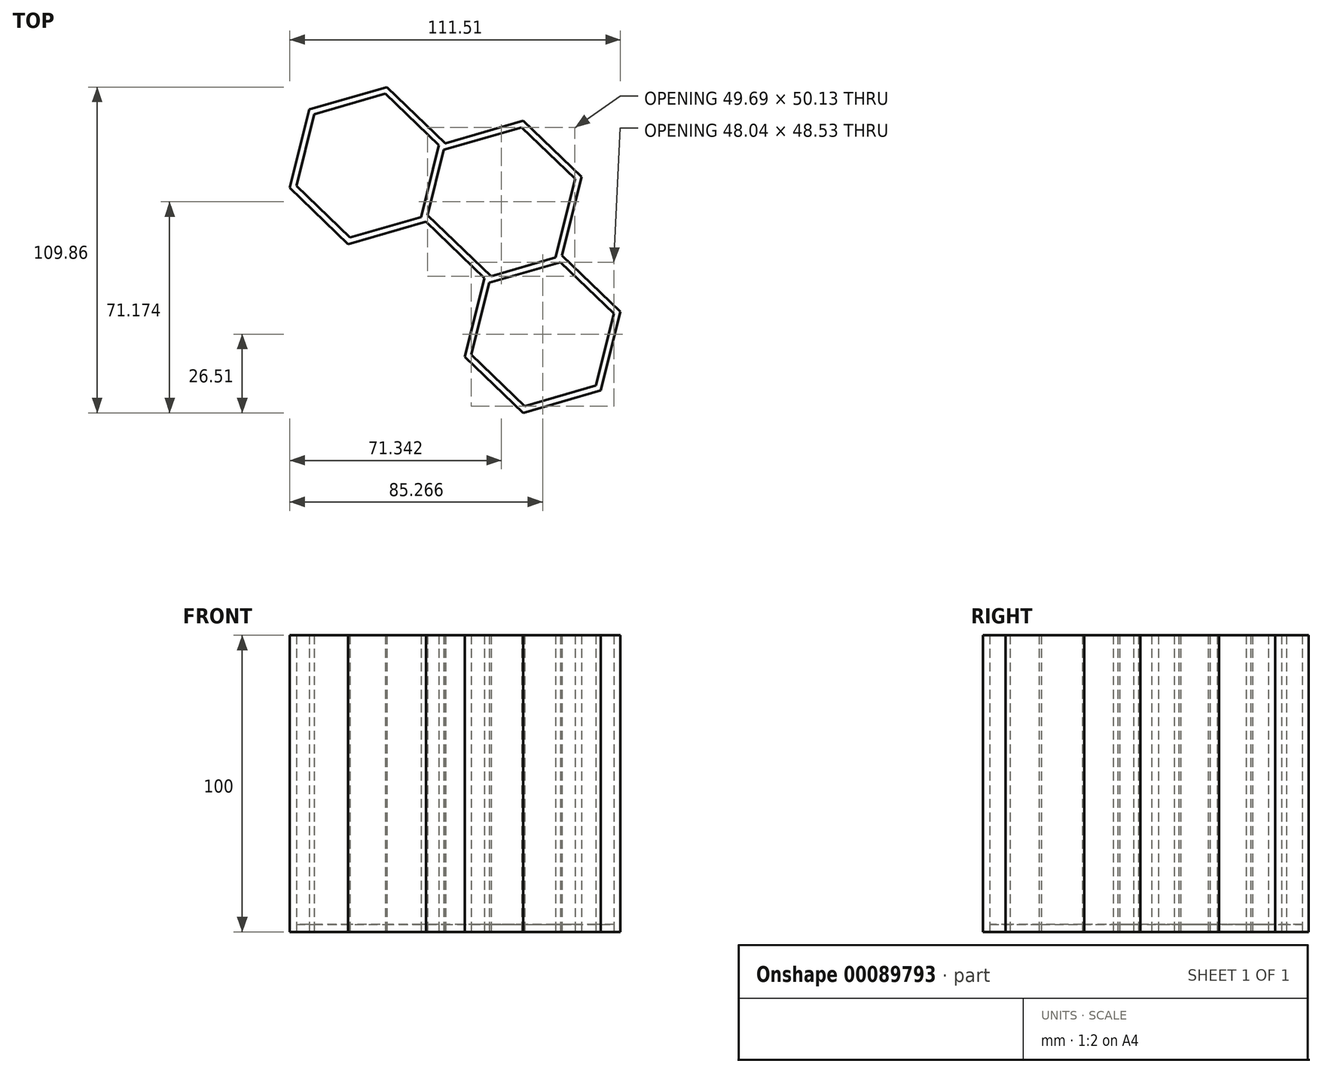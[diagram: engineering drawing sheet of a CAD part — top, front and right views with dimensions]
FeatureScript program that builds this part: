
annotation { "Feature Type Name" : "Feature", "Feature Type Description" : "" }
export const myFeature = defineFeature(function(context is Context, id is Id, definition is map)
    precondition{}
    {
        {
            var Q0;
            Q0=qCreatedBy(makeId("Top.planeOp"),FACE);
            var sketch = newSketch(context, id + "F0", { "sketchPlane" : qUnion([Q0])});
            skLineSegment(sketch, "E0.0", {"start": v(36.55, -2.92) * mm, "end": v(10.37, -10.47) * mm});
            skLineSegment(sketch, "E0.1", {"start": v(10.37, -10.47) * mm, "end": v(-9.34, 8.5) * mm});
            skLineSegment(sketch, "E0.2", {"start": v(-9.34, 8.5) * mm, "end": v(-2.78, 34.98) * mm});
            skLineSegment(sketch, "E0.3", {"start": v(-2.78, 34.98) * mm, "end": v(23.46, 42.54) * mm});
            skLineSegment(sketch, "E0.4", {"start": v(23.46, 42.54) * mm, "end": v(43.12, 23.6) * mm});
            skLineSegment(sketch, "E0.5", {"start": v(43.12, 23.6) * mm, "end": v(36.55, -2.92) * mm});
            skLineSegment(sketch, "E1.0", {"start": v(34.33, -3.56) * mm, "end": v(12.6, -9.83) * mm});
            skLineSegment(sketch, "E1.1", {"start": v(12.6, -9.83) * mm, "end": v(-8.78, 10.75) * mm});
            skLineSegment(sketch, "E1.2", {"start": v(-8.78, 10.75) * mm, "end": v(-3.33, 32.73) * mm});
            skLineSegment(sketch, "E1.3", {"start": v(-3.33, 32.73) * mm, "end": v(22.9, 40.3) * mm});
            skLineSegment(sketch, "E1.4", {"start": v(22.9, 40.3) * mm, "end": v(40.9, 22.97) * mm});
            skLineSegment(sketch, "E1.5", {"start": v(40.9, 22.97) * mm, "end": v(34.33, -3.56) * mm});
            skLineSegment(sketch, "E2.0", {"start": v(-9.34, 8.5) * mm, "end": v(-35.56, 0.95) * mm});
            skLineSegment(sketch, "E2.1", {"start": v(-35.56, 0.95) * mm, "end": v(-55.28, 19.93) * mm});
            skLineSegment(sketch, "E2.2", {"start": v(-55.28, 19.93) * mm, "end": v(-48.73, 46.36) * mm});
            skLineSegment(sketch, "E2.3", {"start": v(-48.73, 46.36) * mm, "end": v(-22.5, 53.92) * mm});
            skLineSegment(sketch, "E2.4", {"start": v(-22.5, 53.92) * mm, "end": v(-2.79, 34.94) * mm});
            skLineSegment(sketch, "E2.5", {"start": v(-2.79, 34.94) * mm, "end": v(-9.34, 8.5) * mm});
            skLineSegment(sketch, "E3.0", {"start": v(-11, 10.1) * mm, "end": v(-35, 3.19) * mm});
            skLineSegment(sketch, "E3.1", {"start": v(-35, 3.19) * mm, "end": v(-53.06, 20.57) * mm});
            skLineSegment(sketch, "E3.2", {"start": v(-53.06, 20.57) * mm, "end": v(-47.07, 44.76) * mm});
            skLineSegment(sketch, "E3.3", {"start": v(-47.07, 44.76) * mm, "end": v(-23.06, 51.68) * mm});
            skLineSegment(sketch, "E3.4", {"start": v(-23.06, 51.68) * mm, "end": v(-5, 34.3) * mm});
            skLineSegment(sketch, "E3.5", {"start": v(-5, 34.3) * mm, "end": v(-11, 10.1) * mm});
            skCircle(sketch, "E4.cCircle", {"center": v(29.99, -29.43) * mm, "radius": 27.3 * mm, "construction": true});
            skLineSegment(sketch, "E4.0", {"start": v(49.66, -48.37) * mm, "end": v(23.42, -55.94) * mm});
            skLineSegment(sketch, "E4.1", {"start": v(23.42, -55.94) * mm, "end": v(3.75, -37) * mm});
            skLineSegment(sketch, "E4.2", {"start": v(3.75, -37) * mm, "end": v(10.31, -10.49) * mm});
            skLineSegment(sketch, "E4.3", {"start": v(10.31, -10.49) * mm, "end": v(36.55, -2.92) * mm});
            skLineSegment(sketch, "E4.4", {"start": v(36.55, -2.92) * mm, "end": v(56.23, -21.86) * mm});
            skLineSegment(sketch, "E4.5", {"start": v(56.23, -21.86) * mm, "end": v(49.66, -48.37) * mm});
            skCircle(sketch, "E5.cCircle", {"center": v(29.99, -29.43) * mm, "radius": 25 * mm, "construction": true});
            skLineSegment(sketch, "E5.0", {"start": v(48, -46.77) * mm, "end": v(23.97, -53.7) * mm});
            skLineSegment(sketch, "E5.1", {"start": v(23.97, -53.7) * mm, "end": v(5.96, -36.36) * mm});
            skLineSegment(sketch, "E5.2", {"start": v(5.96, -36.36) * mm, "end": v(11.98, -12.1) * mm});
            skLineSegment(sketch, "E5.3", {"start": v(11.98, -12.1) * mm, "end": v(36, -5.16) * mm});
            skLineSegment(sketch, "E5.4", {"start": v(36, -5.16) * mm, "end": v(54, -22.5) * mm});
            skLineSegment(sketch, "E5.5", {"start": v(54, -22.5) * mm, "end": v(48, -46.77) * mm});
            skLineSegment(sketch, "E6.0", {"start": v(29.99, -29.43) * mm, "end": v(48, -46.77) * mm, "construction": true});
            skLineSegment(sketch, "E7.0", {"start": v(16.32, 13.78) * mm, "end": v(34.33, -3.56) * mm, "construction": true});
            skLineSegment(sketch, "E8.0", {"start": v(-29, 27.44) * mm, "end": v(-11, 10.1) * mm, "construction": true});
            skSolve(sketch);
        }
        {
            var Q0;
            Q0=makeQuery(id+"F0.imprint","IMPRINT",FACE,{"disambiguationData":[TD([[makeQuery(id+"F0.imprint","IMPRINT",EDGE,{"derivedFrom":sQuery(id+"F0.wireOp",EDGE,"E5.0")}),-1.0]])]});
            var Q1;
            Q1=makeQuery(id+"F0.imprint","IMPRINT",FACE,{"disambiguationData":[TD([[makeQuery(id+"F0.imprint","IMPRINT",EDGE,{"derivedFrom":sQuery(id+"F0.wireOp",EDGE,"E1.0")}),-1.0]])]});
            var Q2;
            Q2=makeQuery(id+"F0.imprint","IMPRINT",FACE,{"disambiguationData":[TD([[makeQuery(id+"F0.imprint","IMPRINT",EDGE,{"derivedFrom":sQuery(id+"F0.wireOp",EDGE,"E3.0")}),-1.0]])]});
            var Q3;
            {var subQ2=sQuery(id+"F0.wireOp",EDGE,"E1.1");Q3=makeQuery(id+"F0.imprint","IMPRINT",FACE,{"disambiguationData":[TD([[makeQuery(id+"F0.imprint","IMPRINT",EDGE,{"derivedFrom":subQ2}),-1.0]])]});}
            extrude(context, id + "F1", {"entities" : qUnion([Q0, Q1, Q2, Q3]), "depth" : 2.5 * mm});
        }
        {
            var Q0;
            {var subQ0=sQuery(id+"F0.wireOp",EDGE,"E0.0");Q0=makeQuery(id+"F0.imprint","IMPRINT",FACE,{"disambiguationData":[TD([[makeQuery(id+"F0.imprint","IMPRINT",EDGE,{"derivedFrom":subQ0}),-1.0]])]});}
            var Q1;
            {var subQ0=sQuery(id+"F0.wireOp",EDGE,"E2.0");Q1=makeQuery(id+"F0.imprint","IMPRINT",FACE,{"disambiguationData":[TD([[makeQuery(id+"F0.imprint","IMPRINT",EDGE,{"derivedFrom":subQ0}),-1.0]])]});}
            var Q2;
            Q2=makeQuery(id+"F0.imprint","IMPRINT",FACE,{"disambiguationData":[TD([[makeQuery(id+"F0.imprint","IMPRINT",EDGE,{"derivedFrom":sQuery(id+"F0.wireOp",EDGE,"E4.0")}),-1.0]])]});
            var Q3;
            {var subQ0=sQuery(id+"F0.wireOp",EDGE,"E0.1");Q3=makeQuery(id+"F0.imprint","IMPRINT",FACE,{"disambiguationData":[TD([[makeQuery(id+"F0.imprint","IMPRINT",EDGE,{"derivedFrom":subQ0}),-1.0]])]});}
            var Q4;
            {var subQ3=sQuery(id+"F0.wireOp",EDGE,"E0.2");Q4=makeQuery(id+"F0.imprint","IMPRINT",FACE,{"disambiguationData":[TD([[makeQuery(id+"F0.imprint","IMPRINT",EDGE,{"derivedFrom":subQ3}),-1.0]])]});}
            extrude(context, id + "F2", {"entities" : qUnion([Q0, Q1, Q2, Q3, Q4]), "depth" : 100 * mm});
        }
    });
